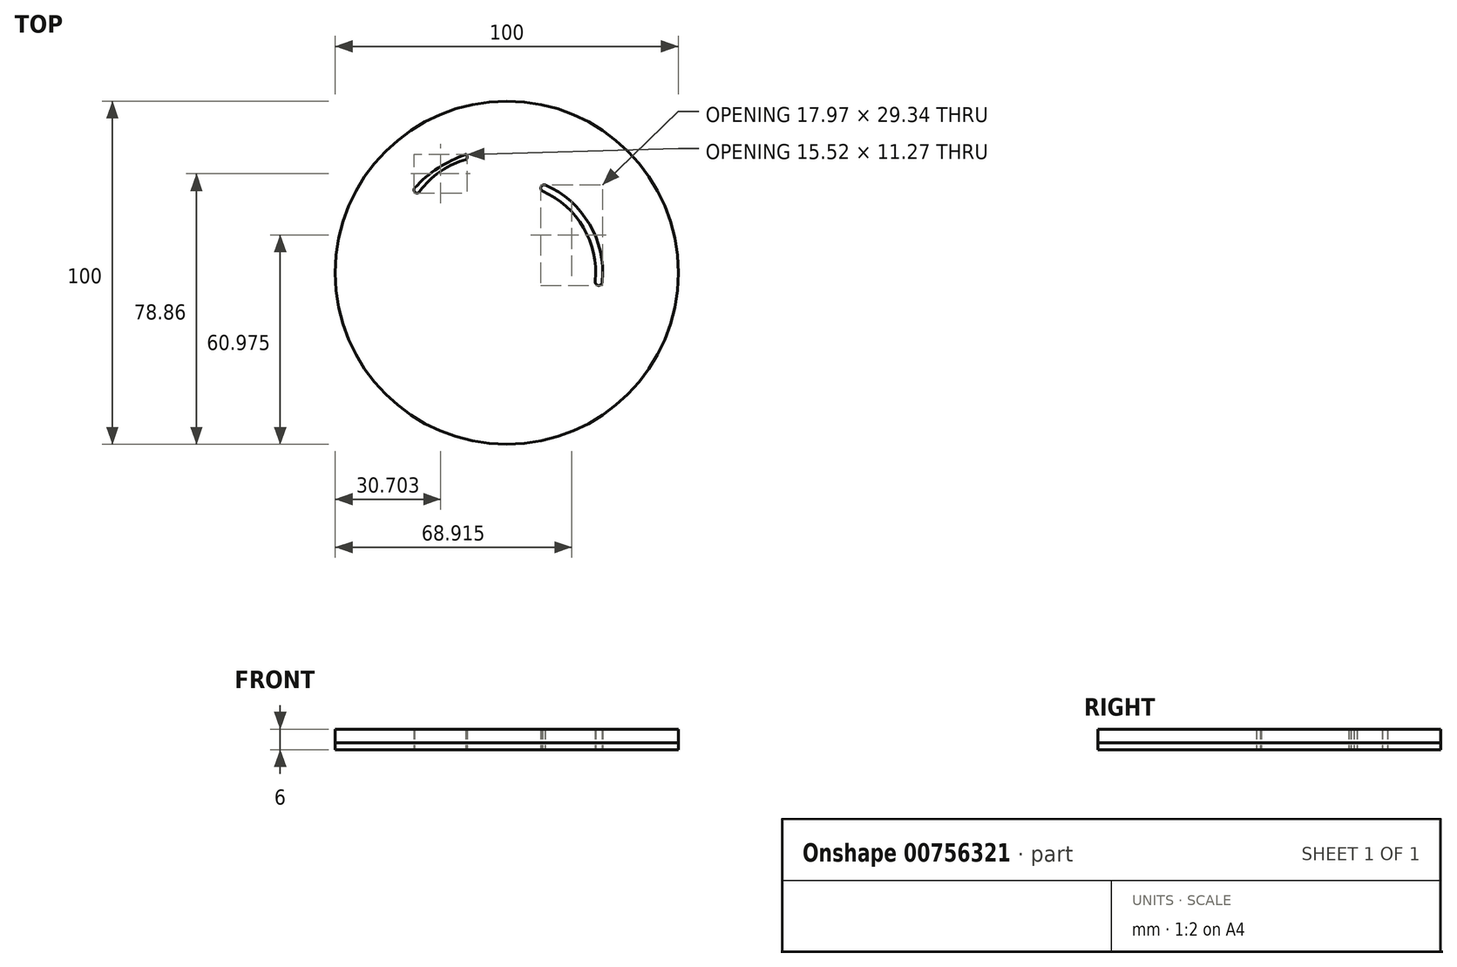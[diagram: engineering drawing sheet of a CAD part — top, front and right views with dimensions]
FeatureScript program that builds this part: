
annotation { "Feature Type Name" : "Feature", "Feature Type Description" : "" }
export const myFeature = defineFeature(function(context is Context, id is Id, definition is map)
    precondition{}
    {
        {
            var Q0;
            Q0=qCreatedBy(makeId("Top.planeOp"),FACE);
            var sketch = newSketch(context, id + "F0", { "sketchPlane" : qUnion([Q0])});
            skCircle(sketch, "E0", {"center": v(0, 0) * mm, "radius": 50 * mm});
            skCircle(sketch, "E1.0", {"center": v(0, 0) * mm, "radius": 48 * mm});
            skLineSegment(sketch, "E2", {"start": v(0, 0) * mm, "end": v(0, 7.94) * mm, "construction": true});
            skLineSegment(sketch, "E3", {"start": v(0, -7.94) * mm, "end": v(0, -48) * mm, "construction": true});
            skLineSegment(sketch, "E4", {"start": v(-48, 0) * mm, "end": v(0, 0) * mm, "construction": true});
            skArc(sketch, "E5", {"start": v(-36.15, 13.2) * mm, "mid": v(-26.16, -28.22) * mm, "end": v(15.89, -35.05) * mm});
            skArc(sketch, "E6.0", {"start": v(-34.5, 11.88) * mm, "mid": v(-36.3, -3.57) * mm, "end": v(-31.52, -18.36) * mm});
            skArc(sketch, "E7", {"start": v(-22.76, 9.79) * mm, "mid": v(-24.71, -1.8) * mm, "end": v(-21.11, -12.97) * mm});
            skArc(sketch, "E8.0", {"start": v(-24.46, 10.54) * mm, "mid": v(-26.62, -0.9) * mm, "end": v(-23.68, -12.19) * mm});
            skArc(sketch, "E9", {"start": v(-8.2, 9.01) * mm, "mid": v(0.03, -12.19) * mm, "end": v(8.15, 9.06) * mm});
            skArc(sketch, "E10.0", {"start": v(-9.6, 10.3) * mm, "mid": v(-0.3, -14.3) * mm, "end": v(9.2, 10.22) * mm});
            skLineSegment(sketch, "E11", {"start": v(8.08, 8.98) * mm, "end": v(8.15, 9.06) * mm, "construction": true});
            skArc(sketch, "E12.trimOffspring", {"start": v(28.17, 26.21) * mm, "mid": v(0.72, 38.48) * mm, "end": v(-27.18, 27.25) * mm});
            skLineSegment(sketch, "E13.trimOffspring", {"start": v(7.95, -9.1) * mm, "end": v(8.02, -9.18) * mm, "construction": true});
            skLineSegment(sketch, "E14.trimOffspring", {"start": v(8.52, -8.56) * mm, "end": v(8.6, -8.63) * mm, "construction": true});
            skArc(sketch, "E15.trimOffspring", {"start": v(28.1, -26.29) * mm, "mid": v(37.56, -8.36) * mm, "end": v(36.6, 11.88) * mm});
            skLineSegment(sketch, "E16.trimOffspring", {"start": v(-27.18, 27.25) * mm, "end": v(-27.22, 27.28) * mm, "construction": true});
            skLineSegment(sketch, "E17.trimOffspring", {"start": v(8.15, 9.06) * mm, "end": v(8.08, 8.98) * mm, "construction": true});
            skLineSegment(sketch, "E18.trimOffspring", {"start": v(-9.1, -7.95) * mm, "end": v(-9.17, -8.02) * mm});
            skArc(sketch, "E19", {"start": v(-11.88, 32.98) * mm, "mid": v(-18.91, 29.84) * mm, "end": v(-24.6, 24.64) * mm});
            skArc(sketch, "E20.0", {"start": v(-11.36, 31.04) * mm, "mid": v(-17.81, 28.16) * mm, "end": v(-23.03, 23.4) * mm});
            skLineSegment(sketch, "E21", {"start": v(-24.6, 24.64) * mm, "end": v(-25.46, 23.56) * mm});
            skArc(sketch, "E22.trimOffspring", {"start": v(-11.88, 34.5) * mm, "mid": v(-19.98, 30.52) * mm, "end": v(-26.87, 24.68) * mm});
            skArc(sketch, "E23", {"start": v(5.7, -1.64) * mm, "mid": v(-4.5, 3.88) * mm, "end": v(2.47, -5.4) * mm});
            skArc(sketch, "E24.0", {"start": v(7.45, -2.75) * mm, "mid": v(-5.82, 5.4) * mm, "end": v(3.3, -7.22) * mm});
            skLineSegment(sketch, "E25.trimOffspring", {"start": v(0, 38.48) * mm, "end": v(0, 38.54) * mm, "construction": true});
            skArc(sketch, "E26.trimOffspring", {"start": v(-3.48, 24.53) * mm, "mid": v(-12.64, 21.32) * mm, "end": v(-19.85, 14.83) * mm});
            skArc(sketch, "E27.trimOffspring", {"start": v(-3.48, 26.4) * mm, "mid": v(-13.52, 22.95) * mm, "end": v(-21.42, 15.83) * mm});
            skLineSegment(sketch, "E28", {"start": v(-24.57, -14.9) * mm, "end": v(-31.52, -18.36) * mm});
            skArc(sketch, "E29.trimOffspring", {"start": v(-30.47, -20.07) * mm, "mid": v(-26.83, -24.72) * mm, "end": v(-22.5, -28.72) * mm});
            skArc(sketch, "E30.trimOffspring", {"start": v(-20.88, -29.92) * mm, "mid": v(-9.26, -35.29) * mm, "end": v(3.5, -36.31) * mm});
            skLineSegment(sketch, "E31", {"start": v(-23.03, 23.4) * mm, "end": v(-23.77, 22.47) * mm});
            skArc(sketch, "E32", {"start": v(-11.36, 31.04) * mm, "mid": v(-9.7, 32.76) * mm, "end": v(-9.75, 35.15) * mm});
            skArc(sketch, "E33", {"start": v(-11.88, 32.98) * mm, "mid": v(-11.54, 33.74) * mm, "end": v(-11.88, 34.5) * mm});
            skArc(sketch, "E34", {"start": v(-26.87, 24.68) * mm, "mid": v(-26.72, 23.41) * mm, "end": v(-25.46, 23.56) * mm});
            skArc(sketch, "E35", {"start": v(-28.3, 26.08) * mm, "mid": v(-27.95, 21.87) * mm, "end": v(-23.77, 22.47) * mm});
            skArc(sketch, "E36", {"start": v(-21.42, 15.83) * mm, "mid": v(-21, 14.77) * mm, "end": v(-19.85, 14.83) * mm});
            skArc(sketch, "E37", {"start": v(-22.76, 9.79) * mm, "mid": v(-23.3, 10.85) * mm, "end": v(-24.46, 10.54) * mm});
            skArc(sketch, "E38", {"start": v(-3.48, 24.53) * mm, "mid": v(-2.8, 25.47) * mm, "end": v(-3.48, 26.4) * mm});
            skArc(sketch, "E39", {"start": v(-34.5, 11.88) * mm, "mid": v(-34.77, 13.23) * mm, "end": v(-36.15, 13.2) * mm});
            skArc(sketch, "E40", {"start": v(-8.2, 9.01) * mm, "mid": v(-8.5, 10.09) * mm, "end": v(-9.6, 10.3) * mm});
            skArc(sketch, "E41", {"start": v(9.2, 10.22) * mm, "mid": v(8.38, 9.9) * mm, "end": v(8.15, 9.06) * mm});
            skArc(sketch, "E42.trimOffspring", {"start": v(5.5, -36.06) * mm, "mid": v(10.28, -35) * mm, "end": v(14.87, -33.31) * mm});
            skArc(sketch, "E43", {"start": v(15.89, -35.05) * mm, "mid": v(16, -33.82) * mm, "end": v(14.87, -33.31) * mm});
            skArc(sketch, "E44", {"start": v(26.62, -24.95) * mm, "mid": v(26.6, -26.47) * mm, "end": v(28.1, -26.29) * mm});
            skPoint(sketch, "E45.orphan", {"position": v(36.2, 4.39) * mm});
            skArc(sketch, "E46", {"start": v(3.3, -7.22) * mm, "mid": v(3.5, -6.02) * mm, "end": v(2.47, -5.4) * mm});
            skArc(sketch, "E47", {"start": v(5.7, -1.64) * mm, "mid": v(5.91, -3.24) * mm, "end": v(7.45, -2.75) * mm});
            skLineSegment(sketch, "E48", {"start": v(-22.5, -28.72) * mm, "end": v(-18.58, -24.2) * mm});
            skArc(sketch, "E49", {"start": v(-14.15, -25.4) * mm, "mid": v(-7.37, -29.06) * mm, "end": v(0.3, -28.46) * mm});
            skArc(sketch, "E50.filletArc", {"start": v(-14.15, -25.4) * mm, "mid": v(-15.64, -24.83) * mm, "end": v(-17.07, -25.52) * mm});
            skArc(sketch, "E51.filletArc", {"start": v(3.01, -30.17) * mm, "mid": v(2.09, -28.64) * mm, "end": v(0.3, -28.46) * mm});
            skArc(sketch, "E52.0", {"start": v(-12.75, -23.99) * mm, "mid": v(-6.96, -27.1) * mm, "end": v(-0.4, -26.6) * mm});
            skArc(sketch, "E53.0", {"start": v(5, -30) * mm, "mid": v(3.16, -26.95) * mm, "end": v(-0.4, -26.6) * mm});
            skArc(sketch, "E54.0", {"start": v(-12.75, -23.99) * mm, "mid": v(-15.71, -22.83) * mm, "end": v(-18.58, -24.2) * mm});
            skPoint(sketch, "E55.visualSharp", {"position": v(-22.69, -13.95) * mm});
            skArc(sketch, "E55.filletArc", {"start": v(-24.57, -14.9) * mm, "mid": v(-23.56, -13.72) * mm, "end": v(-23.68, -12.19) * mm});
            skLineSegment(sketch, "E56", {"start": v(-30.47, -20.07) * mm, "end": v(-21.92, -15.8) * mm});
            skArc(sketch, "E57.filletArc", {"start": v(-21.92, -15.8) * mm, "mid": v(-20.9, -14.57) * mm, "end": v(-21.11, -12.97) * mm});
            skLineSegment(sketch, "E58", {"start": v(-28.3, 26.08) * mm, "end": v(-27.18, 27.25) * mm});
            skArc(sketch, "E59.0", {"start": v(26.71, 24.85) * mm, "mid": v(21.51, 29.47) * mm, "end": v(15.53, 33.01) * mm});
            skArc(sketch, "E60", {"start": v(26.71, 24.85) * mm, "mid": v(28.01, 24.92) * mm, "end": v(28.17, 26.21) * mm});
            skArc(sketch, "E61.0", {"start": v(26.64, -24.92) * mm, "mid": v(28.44, -22.85) * mm, "end": v(30.08, -20.64) * mm});
            skArc(sketch, "E62", {"start": v(36.6, 11.88) * mm, "mid": v(35.47, 12.15) * mm, "end": v(34.7, 11.26) * mm});
            skLineSegment(sketch, "E63.0", {"start": v(35.76, -7.2) * mm, "end": v(35.85, -7.22) * mm});
            skLineSegment(sketch, "E64", {"start": v(18.4, -11.92) * mm, "end": v(31.17, -18.96) * mm});
            skLineSegment(sketch, "E65.0", {"start": v(17.43, -13.67) * mm, "end": v(30.08, -20.64) * mm});
            skArc(sketch, "E66.trimOffspring", {"start": v(31.17, -18.96) * mm, "mid": v(36.24, -4.24) * mm, "end": v(34.7, 11.26) * mm});
            skArc(sketch, "E67", {"start": v(18.4, -11.92) * mm, "mid": v(17.04, -12.32) * mm, "end": v(17.43, -13.67) * mm});
            skArc(sketch, "E68.trimOffspring", {"start": v(13.68, 33.82) * mm, "mid": v(2.07, 36.42) * mm, "end": v(-9.75, 35.15) * mm});
            skArc(sketch, "E69", {"start": v(11.23, 25.6) * mm, "mid": v(24.1, 14.19) * mm, "end": v(27.84, -2.6) * mm});
            skArc(sketch, "E70.0", {"start": v(10.43, 23.77) * mm, "mid": v(22.37, 13.17) * mm, "end": v(25.85, -2.4) * mm});
            skArc(sketch, "E71", {"start": v(13.68, 33.82) * mm, "mid": v(14.61, 33.43) * mm, "end": v(15.53, 33.01) * mm});
            skArc(sketch, "E72", {"start": v(11.23, 25.6) * mm, "mid": v(10.01, 25.05) * mm, "end": v(10.43, 23.77) * mm});
            skArc(sketch, "E73", {"start": v(25.85, -2.4) * mm, "mid": v(26.73, -3.7) * mm, "end": v(27.84, -2.6) * mm});
            skLineSegment(sketch, "E74", {"start": v(-20.88, -29.92) * mm, "end": v(-17.07, -25.52) * mm});
            skLineSegment(sketch, "E75", {"start": v(26.62, -24.95) * mm, "end": v(26.64, -24.92) * mm});
            skArc(sketch, "E76", {"start": v(3.5, -36.31) * mm, "mid": v(4.5, -36.2) * mm, "end": v(5.5, -36.06) * mm});
            skArc(sketch, "E77", {"start": v(3.01, -30.17) * mm, "mid": v(4.07, -30.78) * mm, "end": v(5, -30) * mm});
            skSolve(sketch);
        }
        {
            var Q0;
            Q0 = qSketchRegion(id + "F0", true);
            var Q1;
            Q1=makeQuery(id+"F0.imprint","IMPRINT",FACE,{"disambiguationData":[TD([[makeQuery(id+"F0.imprint","IMPRINT",EDGE,{"derivedFrom":sQuery(id+"F0.wireOp",EDGE,"E26.trimOffspring")}),-1.0]])]});
            var Q2;
            Q2=makeQuery(id+"F0.imprint","IMPRINT",FACE,{"disambiguationData":[TD([[makeQuery(id+"F0.imprint","IMPRINT",EDGE,{"derivedFrom":sQuery(id+"F0.wireOp",EDGE,"E10.0")}),1.0]])]});
            var Q3;
            Q3=makeQuery(id+"F0.imprint","IMPRINT",FACE,{"disambiguationData":[TD([[makeQuery(id+"F0.imprint","IMPRINT",EDGE,{"derivedFrom":sQuery(id+"F0.wireOp",EDGE,"E23")}),-1.0]])]});
            var Q4;
            Q4=makeQuery(id+"F0.imprint","IMPRINT",FACE,{"disambiguationData":[TD([[makeQuery(id+"F0.imprint","IMPRINT",EDGE,{"derivedFrom":sQuery(id+"F0.wireOp",EDGE,"E69")}),-1.0]])]});
            var Q5;
            Q5=makeQuery(id+"F0.imprint","IMPRINT",FACE,{"disambiguationData":[TD([[makeQuery(id+"F0.imprint","IMPRINT",EDGE,{"derivedFrom":sQuery(id+"F0.wireOp",EDGE,"E15.trimOffspring")}),1.0]])]});
            var Q6;
            Q6=makeQuery(id+"F0.imprint","IMPRINT",FACE,{"disambiguationData":[TD([[makeQuery(id+"F0.imprint","IMPRINT",EDGE,{"derivedFrom":sQuery(id+"F0.wireOp",EDGE,"E5")}),1.0]])]});
            var Q7;
            Q7=makeQuery(id+"F0.imprint","IMPRINT",FACE,{"disambiguationData":[TD([[makeQuery(id+"F0.imprint","IMPRINT",EDGE,{"derivedFrom":sQuery(id+"F0.wireOp",EDGE,"E12.trimOffspring")}),1.0]])]});
            extrude(context, id + "F1", {"entities" : qUnion([Q0, Q1, Q2, Q3, Q4, Q5, Q6, Q7]), "depth" : 6 * mm, "offsetDistance" : 25 * mm});
        }
        {
            var Q0;
            Q0=qCreatedBy(makeId("Top.planeOp"),FACE);
            var sketch = newSketch(context, id + "F2", { "sketchPlane" : qUnion([Q0])});
            skCircle(sketch, "E78.0", {"center": v(0, 0) * mm, "radius": 50 * mm});
            skSolve(sketch);
        }
        {
            var Q0;
            Q0 = qSketchRegion(id + "F2", true);
            extrude(context, id + "F3", {"entities" : qUnion([Q0]), "depth" : 2 * mm, "offsetDistance" : 25 * mm});
        }
    });
